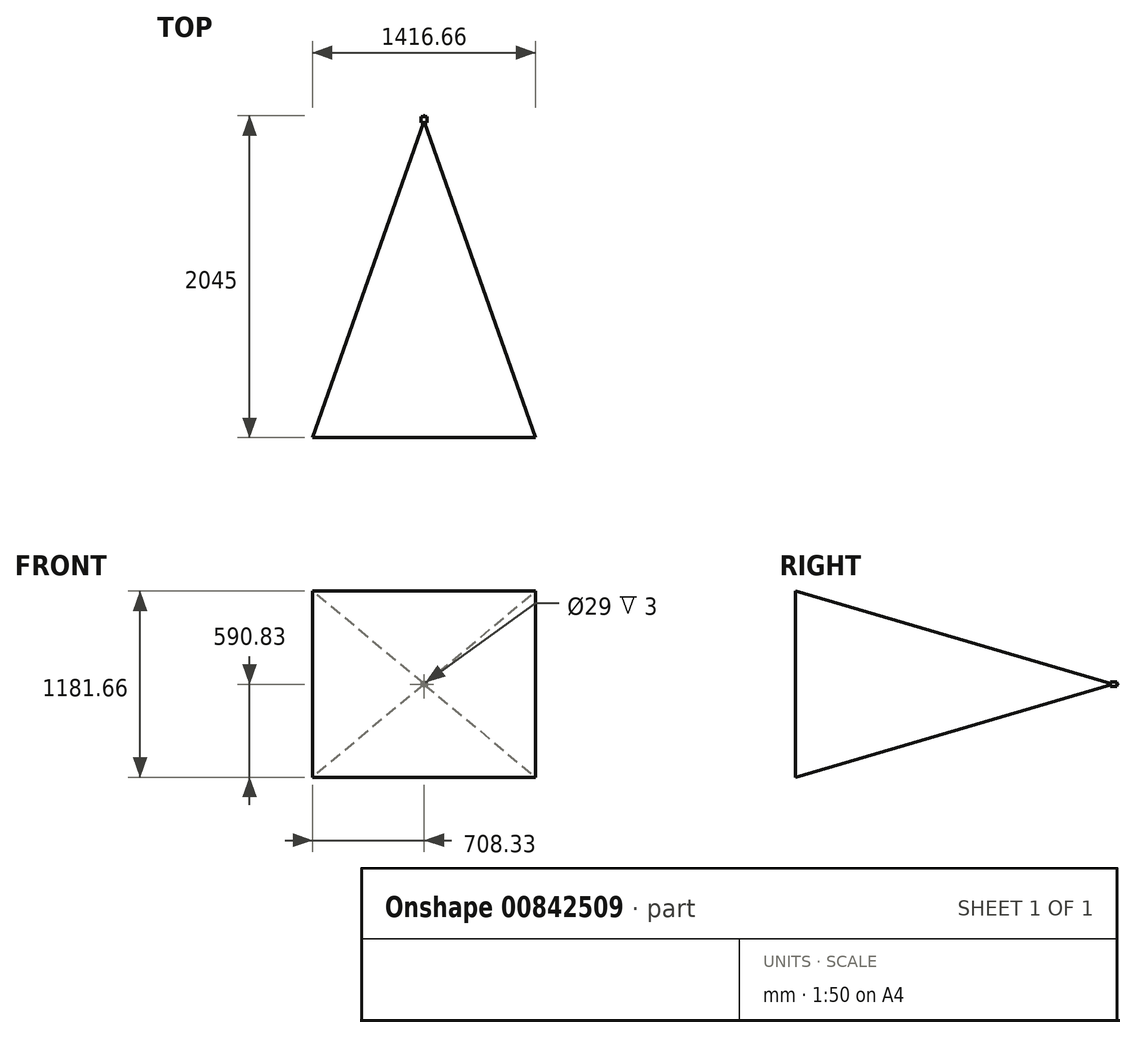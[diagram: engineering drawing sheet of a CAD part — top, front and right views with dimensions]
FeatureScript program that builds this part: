
annotation { "Feature Type Name" : "Feature", "Feature Type Description" : "" }
export const myFeature = defineFeature(function(context is Context, id is Id, definition is map)
    precondition{}
    {
        {
            var Q0;
            Q0=qCreatedBy(makeId("Front.planeOp"),FACE);
            var sketch = newSketch(context, id + "F0", { "sketchPlane" : qUnion([Q0])});
            skLineSegment(sketch, "E0.bottom", {"start": v(20, 15) * mm, "end": v(-20, 15) * mm});
            skLineSegment(sketch, "E0.top", {"start": v(20, -15) * mm, "end": v(-20, -15) * mm});
            skLineSegment(sketch, "E0.left", {"start": v(20, 15) * mm, "end": v(20, -15) * mm});
            skLineSegment(sketch, "E0.right", {"start": v(-20, 15) * mm, "end": v(-20, -15) * mm});
            skPoint(sketch, "E0.middle", {"position": v(0, 0) * mm});
            skSolve(sketch);
        }
        {
            var Q0;
            Q0 = qSketchRegion(id + "F0", true);
            extrude(context, id + "F1", {"entities" : qUnion([Q0]), "depth" : 40 * mm, "offsetDistance" : 25 * mm});
        }
        {
            assignVariable(context, id + "F2", {"name" : "WorkingDistance", "anyValue" : 2000});
        }
        {
            var Q0;
            Q0=makeQuery(id+"F1.opExtrude","CAP_FACE",FACE,{"disambiguationData":[OSD([sQuery(id+"F0.wireOp",EDGE,"E0.bottom"),sQuery(id+"F0.wireOp",EDGE,"E0.top"),sQuery(id+"F0.wireOp",EDGE,"E0.left"),sQuery(id+"F0.wireOp",EDGE,"E0.right")])],"isStart":false});
            var sketch = newSketch(context, id + "F3", { "sketchPlane" : qUnion([Q0])});
            skCircle(sketch, "E1", {"center": v(0, 0) * mm, "radius": 14.5 * mm});
            skSolve(sketch);
        }
        {
            var Q0;
            Q0 = qSketchRegion(id + "F3", true);
            extrude(context, id + "F4", {"entities" : qUnion([Q0]), "operationType" : NewBodyOperationType.REMOVE, "oppositeDirection" : true, "depth" : 3 * mm, "offsetDistance" : 25 * mm});
        }
        {
            var Q0;
            Q0=makeQuery(id+"F4.boolean.opBoolean","COPY",FACE,{"derivedFrom":makeQuery(id+"F4.opExtrude","CAP_FACE",FACE,{"disambiguationData":[OSD([sQuery(id+"F3.wireOp",EDGE,"E1")])],"isStart":false})});
            var sketch = newSketch(context, id + "F5", { "sketchPlane" : qUnion([Q0])});
            skLineSegment(sketch, "E2.bottom", {"start": v(4.25, 3.54) * mm, "end": v(-4.25, 3.54) * mm});
            skLineSegment(sketch, "E2.top", {"start": v(4.25, -3.54) * mm, "end": v(-4.25, -3.54) * mm});
            skLineSegment(sketch, "E2.left", {"start": v(4.25, 3.54) * mm, "end": v(4.25, -3.54) * mm});
            skLineSegment(sketch, "E2.right", {"start": v(-4.25, 3.54) * mm, "end": v(-4.25, -3.54) * mm});
            skPoint(sketch, "E2.middle", {"position": v(0, 0) * mm});
            skSolve(sketch);
        }
        {
            var Q0;
            Q0 = qSketchRegion(id + "F5", true);
            extrude(context, id + "F6", {"entities" : qUnion([Q0]), "operationType" : NewBodyOperationType.ADD, "depth" : 3 * mm, "offsetDistance" : 25 * mm});
        }
        {
            var Q0;
            Q0=makeQuery(id+"F6.opExtrude","CAP_FACE",FACE,{"disambiguationData":[OSD([sQuery(id+"F5.wireOp",EDGE,"E2.bottom"),sQuery(id+"F5.wireOp",EDGE,"E2.top"),sQuery(id+"F5.wireOp",EDGE,"E2.left"),sQuery(id+"F5.wireOp",EDGE,"E2.right")])],"isStart":false});
            cPlane(context, id + "F7", {"entities" : qUnion([Q0]), "cplaneType" : CPlaneType.OFFSET, "offset" : (getVariable(context, 'WorkingDistance')) * mm, "width" : 150 * mm, "height" : 150 * mm});
        }
        {
            var Q0;
            Q0=qCreatedBy(id+"F7.planeOp",FACE);
            var sketch = newSketch(context, id + "F8", { "sketchPlane" : qUnion([Q0])});
            skLineSegment(sketch, "E3.bottom", {"start": v(708.33, 590.83) * mm, "end": v(-708.33, 590.83) * mm});
            skLineSegment(sketch, "E3.top", {"start": v(708.33, -590.83) * mm, "end": v(-708.33, -590.83) * mm});
            skLineSegment(sketch, "E3.left", {"start": v(708.33, 590.83) * mm, "end": v(708.33, -590.83) * mm});
            skLineSegment(sketch, "E3.right", {"start": v(-708.33, 590.83) * mm, "end": v(-708.33, -590.83) * mm});
            skPoint(sketch, "E3.middle", {"position": v(0, 0) * mm});
            skSolve(sketch);
        }
        {
            var Q1;
            Q1=makeQuery(id+"F6.opExtrude","CAP_FACE",FACE,{"disambiguationData":[OSD([sQuery(id+"F5.wireOp",EDGE,"E2.bottom"),sQuery(id+"F5.wireOp",EDGE,"E2.top"),sQuery(id+"F5.wireOp",EDGE,"E2.left"),sQuery(id+"F5.wireOp",EDGE,"E2.right")])],"isStart":false});
            var Q2;
            Q2=makeQuery(id+"F8.imprint","IMPRINT",FACE,{"disambiguationData":[TD([[makeQuery(id+"F8.imprint","IMPRINT",EDGE,{"derivedFrom":sQuery(id+"F8.wireOp",EDGE,"E3.bottom")}),1.0]])]});
            loft(context, id + "F9", {"operationType" : NewBodyOperationType.ADD, "sheetProfilesArray" : [{ "sheetProfileEntities" : qUnion([Q1]) }, { "sheetProfileEntities" : qUnion([Q2]) }]});
        }
        {
            var Q0;
            Q0=makeQuery(id+"F0.imprint","IMPRINT",FACE,{"disambiguationData":[TD([[makeQuery(id+"F0.imprint","IMPRINT",EDGE,{"derivedFrom":sQuery(id+"F0.wireOp",EDGE,"E0.bottom")}),1.0]])]});
            var sketch = newSketch(context, id + "F10", { "sketchPlane" : qUnion([Q0])});
            skArc(sketch, "E4", {"start": v(0, 5) * mm, "mid": v(5, 0) * mm, "end": v(0, -5) * mm});
            skLineSegment(sketch, "E5", {"start": v(0, 5) * mm, "end": v(0, -5) * mm});
            skSolve(sketch);
        }
        {
            var Q0;
            Q0 = qSketchRegion(id + "F10", true);
            var Q1;
            Q1=sQuery(id+"F10.wireOp",EDGE,"E5");
            revolve(context, id + "F11", {"operationType" : NewBodyOperationType.ADD, "surfaceOperationType" : NewSurfaceOperationType.NEW, "entities" : qUnion([Q0]), "axis" : qUnion([Q1]), "revolveType" : RevolveType.FULL});
        }
    });
